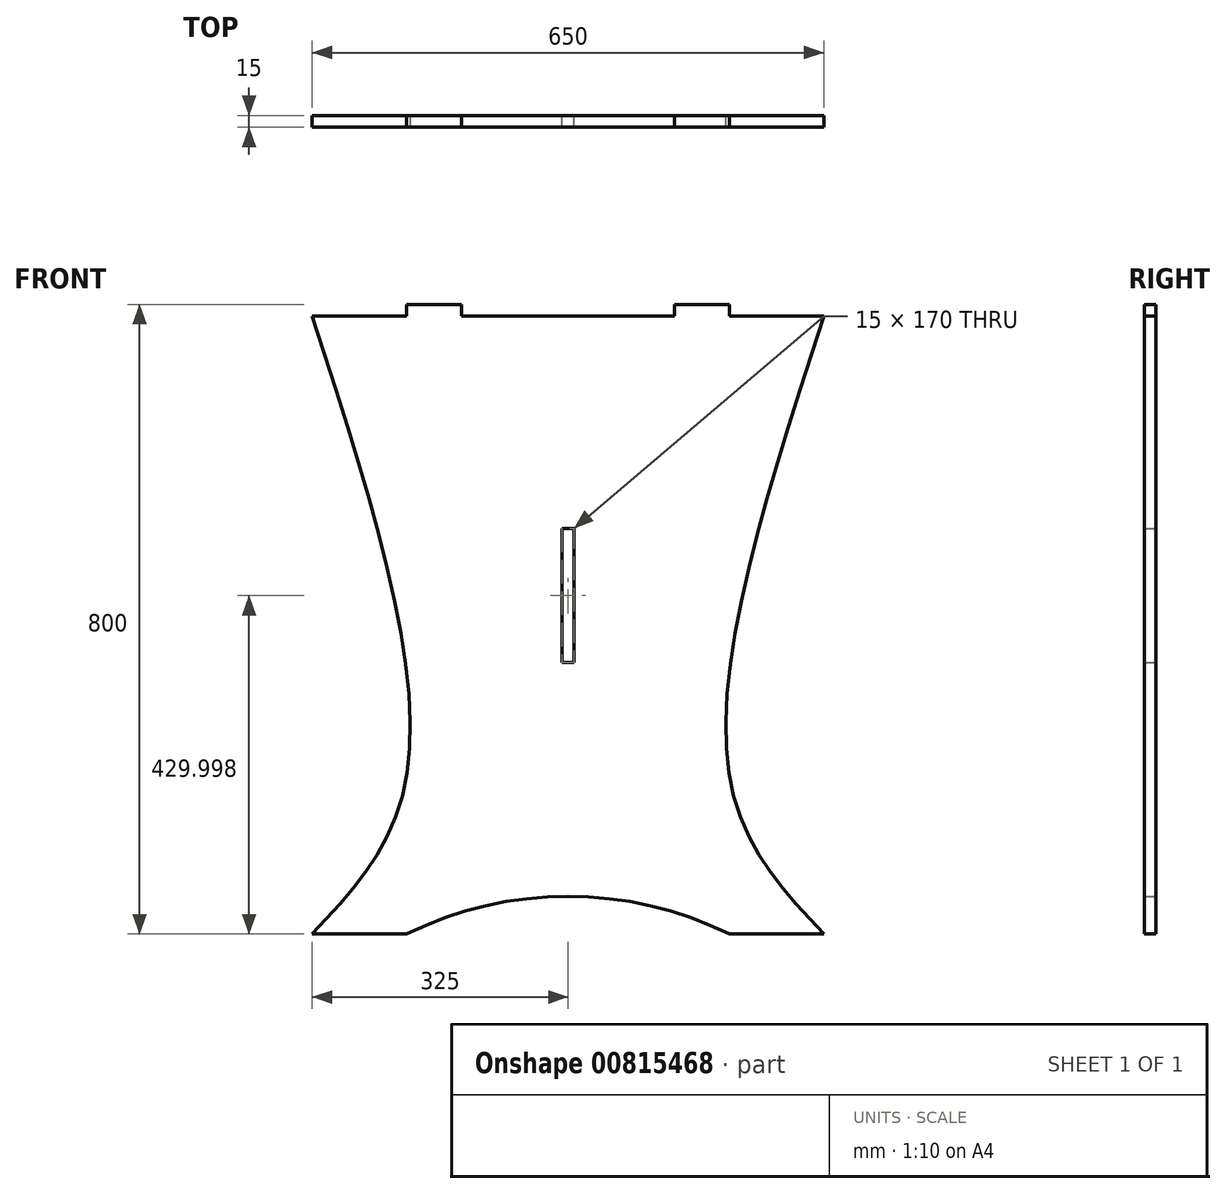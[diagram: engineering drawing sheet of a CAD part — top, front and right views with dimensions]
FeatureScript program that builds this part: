
annotation { "Feature Type Name" : "Feature", "Feature Type Description" : "" }
export const myFeature = defineFeature(function(context is Context, id is Id, definition is map)
    precondition{}
    {
        {
            var Q0;
            Q0=qCreatedBy(makeId("Front.planeOp"),FACE);
            var sketch = newSketch(context, id + "F0", { "sketchPlane" : qUnion([Q0])});
            skLineSegment(sketch, "E0.bottom", {"start": v(-205, 400) * mm, "end": v(-135, 400) * mm});
            skLineSegment(sketch, "E0.top", {"start": v(-325, -400) * mm, "end": v(-205, -400) * mm});
            skPoint(sketch, "E0.middle", {"position": v(0, 0) * mm});
            skLineSegment(sketch, "E1.top", {"start": v(-325, 385) * mm, "end": v(-205, 385) * mm});
            skLineSegment(sketch, "E1.right", {"start": v(-205, 400) * mm, "end": v(-205, 385) * mm});
            skPoint(sketch, "E2.orphan", {"position": v(-325, 400) * mm});
            skLineSegment(sketch, "E3.right", {"start": v(-135, 400) * mm, "end": v(-135, 385) * mm});
            skLineSegment(sketch, "E4.top", {"start": v(325, 385) * mm, "end": v(205, 385) * mm});
            skLineSegment(sketch, "E4.right", {"start": v(205, 400) * mm, "end": v(205, 385) * mm});
            skPoint(sketch, "E5.orphan", {"position": v(325, 400) * mm});
            skLineSegment(sketch, "E6.bottom", {"start": v(205, 400) * mm, "end": v(135, 400) * mm});
            skLineSegment(sketch, "E6.right", {"start": v(135, 400) * mm, "end": v(135, 385) * mm});
            skLineSegment(sketch, "E7", {"start": v(-135, 385) * mm, "end": v(135, 385) * mm});
            skLineSegment(sketch, "E8.trimOffspring", {"start": v(135, 400) * mm, "end": v(205, 400) * mm});
            skFitSpline(sketch, "E9", {"points": [v(-325, 385) * mm, v(-205, -200) * mm, v(-325, -400) * mm], "startDerivative": vector(351, -1083.08) * mm, "endDerivative": vector(-409.51, -437.23) * mm});
            skLineSegment(sketch, "E10.bottom", {"start": v(325, -400) * mm, "end": v(205, -400) * mm});
            skFitSpline(sketch, "E11", {"points": [v(325, 385) * mm, v(205, -200) * mm, v(325, -400) * mm], "startDerivative": vector(-351, -1083.08) * mm, "endDerivative": vector(409.51, -437.23) * mm});
            skArc(sketch, "E12", {"start": v(205, -400) * mm, "mid": v(0, -352.03) * mm, "end": v(-205, -400) * mm});
            skLineSegment(sketch, "E13.trimOffspring", {"start": v(205, -400) * mm, "end": v(325, -400) * mm});
            skPoint(sketch, "E14.bottom.start.orphan", {"position": v(-6.37, 85) * mm});
            skPoint(sketch, "E14.top.end.orphan", {"position": v(6.37, -85) * mm});
            skPoint(sketch, "E15.orphan", {"position": v(7.5, 85) * mm});
            skPoint(sketch, "E16.bottom.start.orphan", {"position": v(-7.5, 85) * mm});
            skPoint(sketch, "E17.orphan", {"position": v(-7.5, -85) * mm});
            skPoint(sketch, "E16.top.end.orphan", {"position": v(7.5, -85) * mm});
            skLineSegment(sketch, "E18.bottom", {"start": v(-7.5, 115) * mm, "end": v(7.5, 115) * mm});
            skLineSegment(sketch, "E18.top", {"start": v(-7.5, -55) * mm, "end": v(7.5, -55) * mm});
            skLineSegment(sketch, "E18.left", {"start": v(-7.5, 115) * mm, "end": v(-7.5, -55) * mm});
            skLineSegment(sketch, "E18.right", {"start": v(7.5, 115) * mm, "end": v(7.5, -55) * mm});
            skLineSegment(sketch, "E19", {"start": v(325, -400) * mm, "end": v(325, -482.25) * mm});
            skLineSegment(sketch, "E20", {"start": v(-325, -400) * mm, "end": v(-325, -487.2) * mm});
            skSolve(sketch);
        }
        {
            var Q0;
            Q0=qSketchRegion(id+"F0",true);
            extrude(context, id + "F1", {"entities" : qUnion([Q0]), "depth" : 15 * mm, "offsetDistance" : 25.4 * mm});
        }
    });
